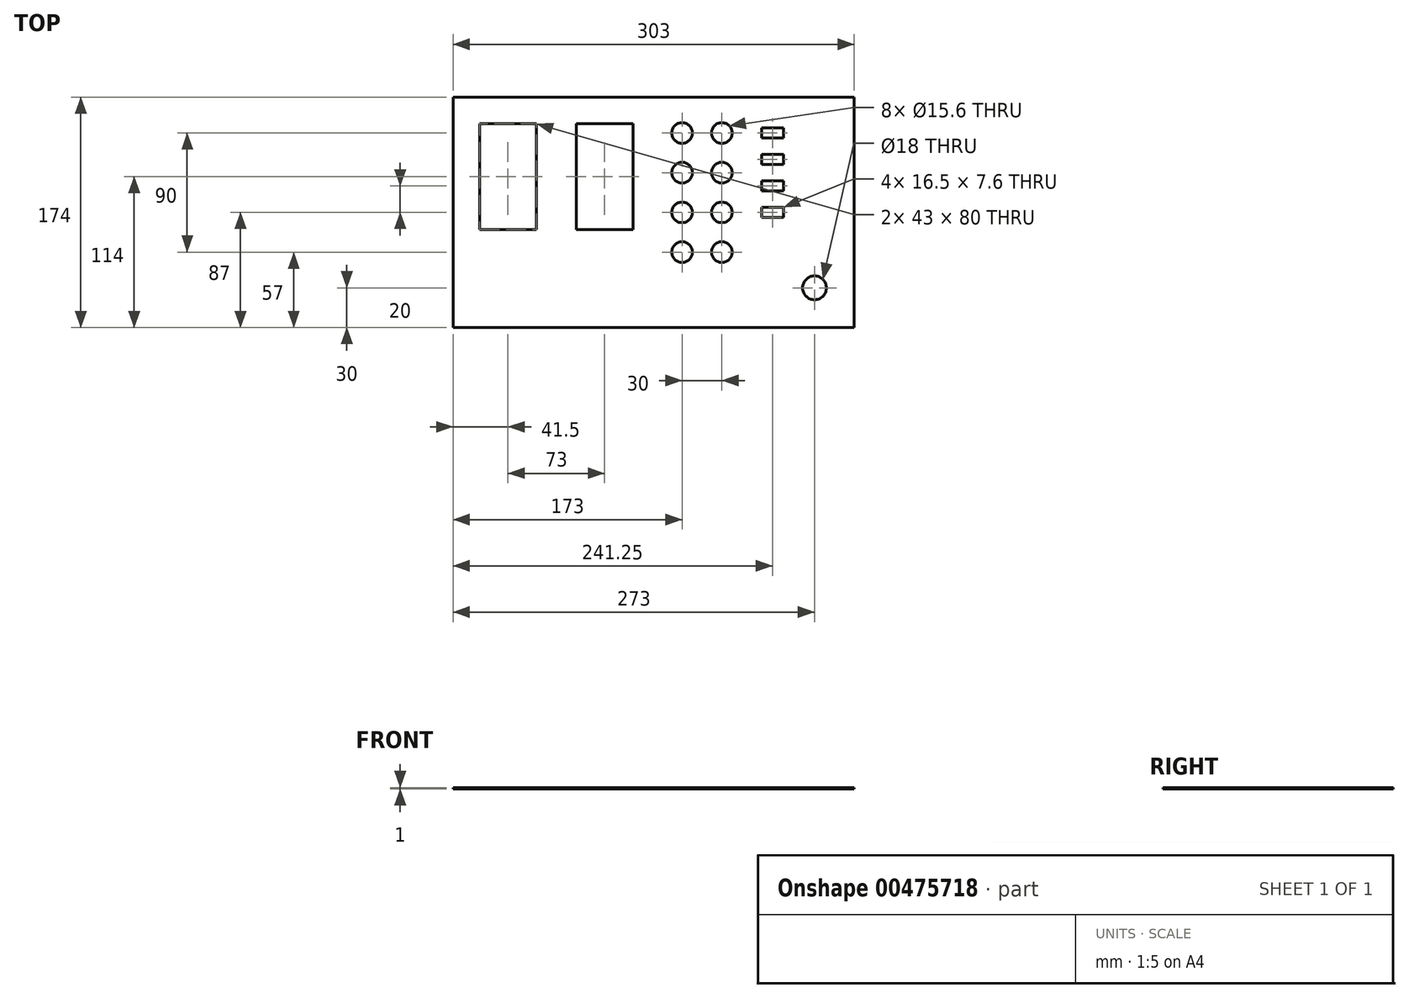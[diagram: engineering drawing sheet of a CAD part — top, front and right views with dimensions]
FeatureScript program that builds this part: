
annotation { "Feature Type Name" : "Feature", "Feature Type Description" : "" }
export const myFeature = defineFeature(function(context is Context, id is Id, definition is map)
    precondition{}
    {
        {
            var Q0;
            Q0=qCreatedBy(makeId("Top.planeOp"),FACE);
            var sketch = newSketch(context, id + "F0", { "sketchPlane" : qUnion([Q0])});
            skLineSegment(sketch, "E0.bottom", {"start": v(-151.5, 87) * mm, "end": v(151.5, 87) * mm});
            skLineSegment(sketch, "E0.top", {"start": v(-151.5, -87) * mm, "end": v(151.5, -87) * mm});
            skLineSegment(sketch, "E0.left", {"start": v(-151.5, 87) * mm, "end": v(-151.5, -87) * mm});
            skLineSegment(sketch, "E0.right", {"start": v(151.5, 87) * mm, "end": v(151.5, -87) * mm});
            skCircle(sketch, "E1", {"center": v(51.5, 60) * mm, "radius": 7.8 * mm});
            skCircle(sketch, "E2", {"center": v(51.5, 30) * mm, "radius": 7.8 * mm});
            skCircle(sketch, "E3", {"center": v(51.5, 0) * mm, "radius": 7.8 * mm});
            skCircle(sketch, "E4", {"center": v(51.5, -30) * mm, "radius": 7.8 * mm});
            skCircle(sketch, "E5", {"center": v(21.5, 60) * mm, "radius": 7.8 * mm});
            skCircle(sketch, "E6", {"center": v(21.5, 30) * mm, "radius": 7.8 * mm});
            skCircle(sketch, "E7", {"center": v(21.5, 0) * mm, "radius": 7.8 * mm});
            skCircle(sketch, "E8", {"center": v(21.5, -30) * mm, "radius": 7.8 * mm});
            skLineSegment(sketch, "E9.bottom", {"start": v(-131.5, 67) * mm, "end": v(-88.5, 67) * mm});
            skLineSegment(sketch, "E9.top", {"start": v(-131.5, -13) * mm, "end": v(-88.5, -13) * mm});
            skLineSegment(sketch, "E9.left", {"start": v(-131.5, 67) * mm, "end": v(-131.5, -13) * mm});
            skLineSegment(sketch, "E9.right", {"start": v(-88.5, 67) * mm, "end": v(-88.5, -13) * mm});
            skLineSegment(sketch, "E10.bottom", {"start": v(-128, 53.25) * mm, "end": v(-92, 53.25) * mm});
            skLineSegment(sketch, "E10.top", {"start": v(-128, 0.75) * mm, "end": v(-92, 0.75) * mm});
            skLineSegment(sketch, "E10.left", {"start": v(-128, 53.25) * mm, "end": v(-128, 0.75) * mm});
            skLineSegment(sketch, "E10.right", {"start": v(-92, 53.25) * mm, "end": v(-92, 0.75) * mm});
            skCircle(sketch, "E11", {"center": v(-125.5, 62) * mm, "radius": 3 * mm});
            skPoint(sketch, "E12", {"position": v(-110, 53.25) * mm});
            skCircle(sketch, "E13.MirrorC", {"center": v(-94.5, 62) * mm, "radius": 3 * mm});
            skPoint(sketch, "E14", {"position": v(-128, 53.25) * mm});
            skPoint(sketch, "E15", {"position": v(-128, 27) * mm});
            skCircle(sketch, "E16.MirrorC", {"center": v(-94.5, -8) * mm, "radius": 3 * mm});
            skCircle(sketch, "E17.MirrorC", {"center": v(-125.5, -8) * mm, "radius": 3 * mm});
            skPoint(sketch, "E18.left.start.orphan", {"position": v(-63.5, 67) * mm});
            skLineSegment(sketch, "E19.bottom", {"start": v(-58.5, 67) * mm, "end": v(-15.5, 67) * mm});
            skLineSegment(sketch, "E19.top", {"start": v(-58.5, -13) * mm, "end": v(-15.5, -13) * mm});
            skLineSegment(sketch, "E19.left", {"start": v(-58.5, 67) * mm, "end": v(-58.5, -13) * mm});
            skLineSegment(sketch, "E19.right", {"start": v(-15.5, 67) * mm, "end": v(-15.5, -13) * mm});
            skLineSegment(sketch, "E20.bottom", {"start": v(-55, 53.25) * mm, "end": v(-19, 53.25) * mm});
            skLineSegment(sketch, "E20.top", {"start": v(-55, 0.75) * mm, "end": v(-19, 0.75) * mm});
            skLineSegment(sketch, "E20.left", {"start": v(-55, 53.25) * mm, "end": v(-55, 0.75) * mm});
            skLineSegment(sketch, "E20.right", {"start": v(-19, 53.25) * mm, "end": v(-19, 0.75) * mm});
            skCircle(sketch, "E21", {"center": v(-52.5, 62) * mm, "radius": 3 * mm});
            skPoint(sketch, "E22", {"position": v(-37, 53.25) * mm});
            skCircle(sketch, "E23.MirrorC", {"center": v(-21.5, 62) * mm, "radius": 3 * mm});
            skPoint(sketch, "E24", {"position": v(-55, 53.25) * mm});
            skPoint(sketch, "E25", {"position": v(-55, 27) * mm});
            skCircle(sketch, "E26.MirrorC", {"center": v(-21.5, -8) * mm, "radius": 3 * mm});
            skCircle(sketch, "E27.MirrorC", {"center": v(-52.5, -8) * mm, "radius": 3 * mm});
            skCircle(sketch, "E28", {"center": v(121.5, -57) * mm, "radius": 9 * mm});
            skLineSegment(sketch, "E29.bottom", {"start": v(81.5, 63.8) * mm, "end": v(98, 63.8) * mm});
            skLineSegment(sketch, "E29.top", {"start": v(81.5, 56.2) * mm, "end": v(98, 56.2) * mm});
            skLineSegment(sketch, "E29.left", {"start": v(81.5, 63.8) * mm, "end": v(81.5, 56.2) * mm});
            skLineSegment(sketch, "E29.right", {"start": v(98, 63.8) * mm, "end": v(98, 56.2) * mm});
            skPoint(sketch, "E30", {"position": v(81.5, 60) * mm});
            skLineSegment(sketch, "E31.0.1.0", {"start": v(81.5, 43.8) * mm, "end": v(81.5, 36.2) * mm});
            skLineSegment(sketch, "E31.0.1.1", {"start": v(81.5, 43.8) * mm, "end": v(98, 43.8) * mm});
            skLineSegment(sketch, "E31.0.1.2", {"start": v(81.5, 36.2) * mm, "end": v(98, 36.2) * mm});
            skLineSegment(sketch, "E31.0.1.3", {"start": v(98, 43.8) * mm, "end": v(98, 36.2) * mm});
            skLineSegment(sketch, "E31.0.2.0", {"start": v(81.5, 23.8) * mm, "end": v(81.5, 16.2) * mm});
            skLineSegment(sketch, "E31.0.2.1", {"start": v(81.5, 23.8) * mm, "end": v(98, 23.8) * mm});
            skLineSegment(sketch, "E31.0.2.2", {"start": v(81.5, 16.2) * mm, "end": v(98, 16.2) * mm});
            skLineSegment(sketch, "E31.0.2.3", {"start": v(98, 23.8) * mm, "end": v(98, 16.2) * mm});
            skLineSegment(sketch, "E31.0.3.0", {"start": v(81.5, 3.8) * mm, "end": v(81.5, -3.8) * mm});
            skLineSegment(sketch, "E31.0.3.1", {"start": v(81.5, 3.8) * mm, "end": v(98, 3.8) * mm});
            skLineSegment(sketch, "E31.0.3.2", {"start": v(81.5, -3.8) * mm, "end": v(98, -3.8) * mm});
            skLineSegment(sketch, "E31.0.3.3", {"start": v(98, 3.8) * mm, "end": v(98, -3.8) * mm});
            skLineSegment(sketch, "E31.direction1", {"start": v(81.5, 56.2) * mm, "end": v(114.5, 56.2) * mm, "construction": true});
            skLineSegment(sketch, "E31.direction2", {"start": v(81.5, 56.2) * mm, "end": v(81.5, 36.2) * mm, "construction": true});
            skSolve(sketch);
        }
        {
            var Q0;
            Q0=makeQuery(id+"F0.imprint","IMPRINT",FACE,{"disambiguationData":[TD([[makeQuery(id+"F0.imprint","IMPRINT",EDGE,{"derivedFrom":sQuery(id+"F0.wireOp",EDGE,"E0.bottom")}),-1.0]])]});
            extrude(context, id + "F1", {"entities" : qUnion([Q0]), "depth" : 1 * mm});
        }
    });
